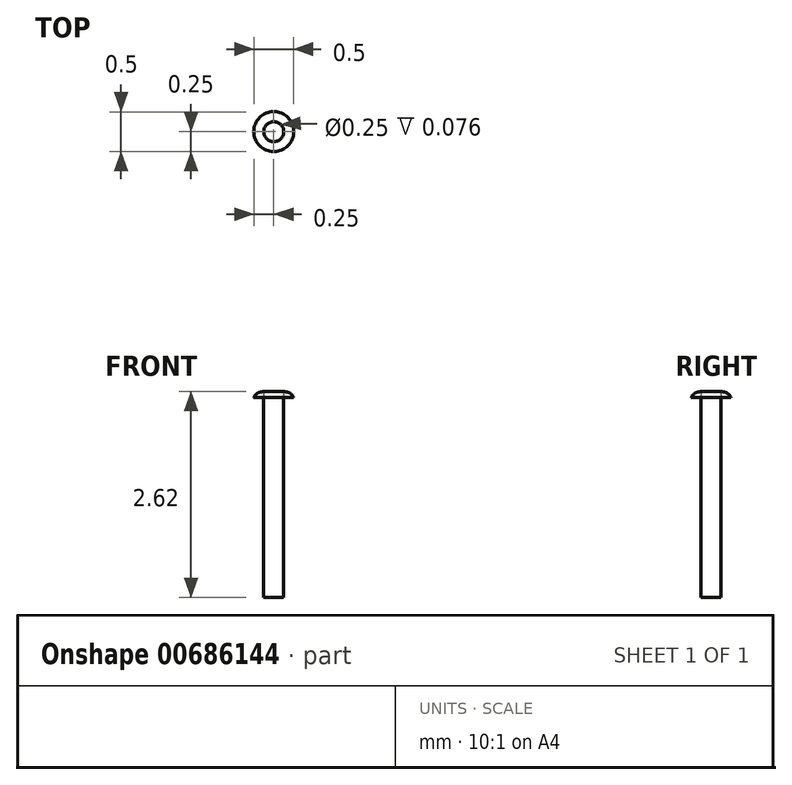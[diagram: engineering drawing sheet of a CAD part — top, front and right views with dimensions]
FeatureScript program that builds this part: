
annotation { "Feature Type Name" : "Feature", "Feature Type Description" : "" }
export const myFeature = defineFeature(function(context is Context, id is Id, definition is map)
    precondition{}
    {
        {
            var Q0;
            Q0=qCreatedBy(makeId("Top.planeOp"),FACE);
            var sketch = newSketch(context, id + "F0", { "sketchPlane" : qUnion([Q0])});
            skCircle(sketch, "E0", {"center": v(0, 0) * mm, "radius": 0.13 * mm});
            skSolve(sketch);
        }
        {
            var Q0;
            Q0=makeQuery(id+"F0.imprint","IMPRINT",FACE,{"disambiguationData":[TD([[makeQuery(id+"F0.imprint","IMPRINT",EDGE,{"derivedFrom":sQuery(id+"F0.wireOp",EDGE,"E0")}),1.0]])]});
            extrude(context, id + "F1", {"entities" : qUnion([Q0]), "depth" : 2.54 * mm, "offsetDistance" : 25.4 * mm});
        }
        {
            var Q0;
            Q0=makeQuery(id+"F1.opExtrude","CAP_FACE",FACE,{"disambiguationData":[OSD([sQuery(id+"F0.wireOp",EDGE,"E0")])],"isStart":false});
            var sketch = newSketch(context, id + "F2", { "sketchPlane" : qUnion([Q0])});
            skCircle(sketch, "E1", {"center": v(0, 0) * mm, "radius": 0.25 * mm});
            skSolve(sketch);
        }
        {
            var Q0;
            Q0=makeQuery(id+"F2.imprint","IMPRINT",FACE,{"disambiguationData":[TD([[makeQuery(id+"F2.imprint","IMPRINT",EDGE,{"derivedFrom":sQuery(id+"F2.wireOp",EDGE,"E1")}),1.0]])]});
            extrude(context, id + "F3", {"entities" : qUnion([Q0]), "depth" : 0.08 * mm, "offsetDistance" : 25.4 * mm});
        }
        {
            var Q0;
            Q0=makeQuery(id+"F1.opExtrude","CAP_FACE",FACE,{"disambiguationData":[OSD([sQuery(id+"F0.wireOp",EDGE,"E0")])],"isStart":false});
            extrude(context, id + "F4", {"entities" : qUnion([Q0]), "depth" : 0.08 * mm, "offsetDistance" : 25.4 * mm});
        }
        {
            var Q0;
            Q0=makeQuery(id+"F3.opExtrude","CAP_EDGE",EDGE,{"disambiguationData":[OSD([sQuery(id+"F2.wireOp",EDGE,"E1")])],"isStart":false});
            fillet(context, id + "F5", {"entities" : qUnion([Q0]), "radius" : 0.13 * mm, "tangentPropagation" : true, "allowEdgeOverflow" : false});
        }
    });
